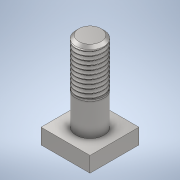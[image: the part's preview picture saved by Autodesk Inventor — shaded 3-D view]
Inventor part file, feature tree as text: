
AUTODESK INVENTOR PART (.ipt)
format: ipt  version: 2020 (Build 240168000, 168)  size: 919,040 bytes
history: native  units: in
note: dims shown in document units (in); Inventor stores cm internally (conversion verified against a paired STEP export)
features: sketch x5, extrude x2, revolve x2, chamfer x1, thread x1, helix x1
ambient origin geometry x8: Origin, YZ Plane, XZ Plane, XY Plane, X Axis, Y Axis, Z Axis, Center Point
bodies: Solid1 (feature_tree), Solid2 (feature_tree)
feature tree (12):
  extrude  "Extrusion1"  Depth=0.3438in TaperAngle=0.0deg
  extrude  "Extrusion2"  Depth=1.0in TaperAngle=0.0deg
  chamfer  "Chamfer1"  Distance=0.0625in Angle=45.0deg
  thread  "Thread1"  [1 undecoded]
  revolve  "Revolution1"  [1 undecoded]
  revolve  "Revolution2"  [1 undecoded]
  helix  "Coil1"  [1 undecoded]
  sketch  "Sketch1"  dims[d0=1.0938in d2=0.3438in d3=0.0in]
  sketch  "Sketch2"  dims[d4=0.625in d5=1.7812in d6=0.0in d7=0.0625in d8=0.125in d9=45.0deg d10=1.0in d11=0.0in]
  sketch  "Sketch3"  dims[d12=0.3779in d13=0.0146in d14=0.0146in d17=0.0909in]
  sketch  "Sketch4"  dims[d19=0.3779in d21=0.0in d22=0.0in]
  sketch  "Sketch5"  dims[d23=0.091in d24=1.1818in d25=0.3937in d26=0.0in d27=0.0in d28=0.0in d29=0.0in d30=0.0in]
note: 4 required parameter values undecoded (feature->parameter linkage not recoverable at this tier; creation-order binding heuristic only, values carry confidence <= 0.55)